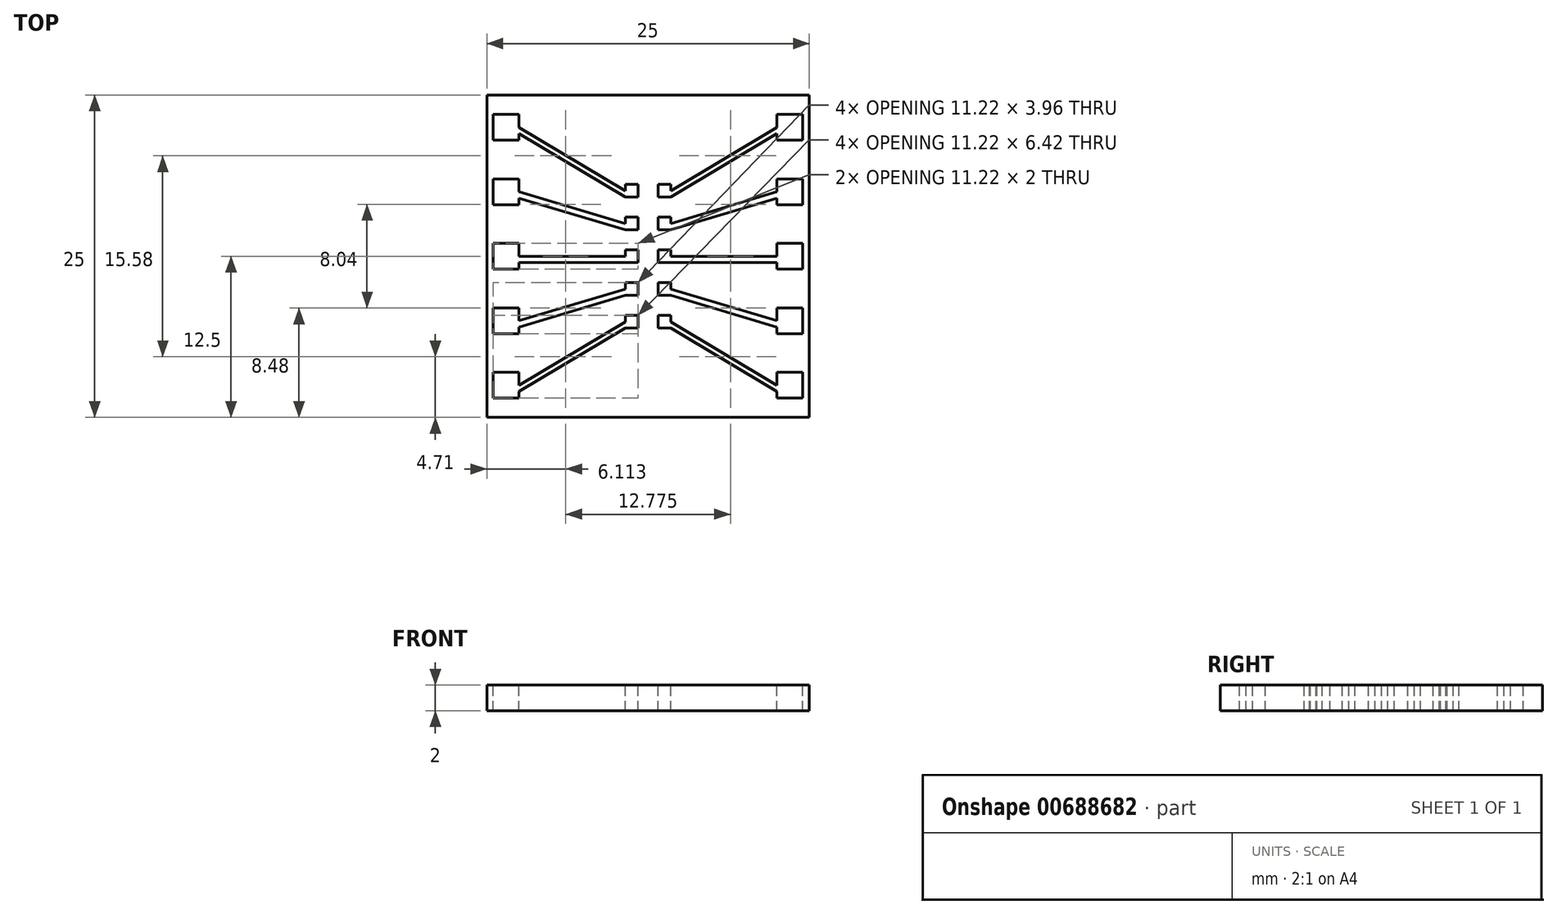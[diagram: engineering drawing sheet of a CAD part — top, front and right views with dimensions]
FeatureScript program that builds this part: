
annotation { "Feature Type Name" : "Feature", "Feature Type Description" : "" }
export const myFeature = defineFeature(function(context is Context, id is Id, definition is map)
    precondition{}
    {
        {
            var Q0;
            Q0=qCreatedBy(makeId("Top.planeOp"),FACE);
            var sketch = newSketch(context, id + "F0", { "sketchPlane" : qUnion([Q0])});
            skLineSegment(sketch, "E0.bottom", {"start": v(0, 0) * mm, "end": v(-25, 0) * mm});
            skLineSegment(sketch, "E0.top", {"start": v(0, 25) * mm, "end": v(-25, 25) * mm});
            skLineSegment(sketch, "E0.left", {"start": v(0, 0) * mm, "end": v(0, 25) * mm});
            skLineSegment(sketch, "E0.right", {"start": v(-25, 0) * mm, "end": v(-25, 25) * mm});
            skSolve(sketch);
        }
        {
            var Q0;
            Q0=makeQuery(id+"F0.imprint","IMPRINT",FACE,{"disambiguationData":[TD([[makeQuery(id+"F0.imprint","IMPRINT",EDGE,{"derivedFrom":sQuery(id+"F0.wireOp",EDGE,"E0.bottom")}),-1.0]])]});
            var Q1;
            Q1 = qSketchRegion(id + "F2", true);
            extrude(context, id + "F1", {"entities" : qUnion([Q0, Q1]), "depth" : 2 * mm, "offsetDistance" : 25 * mm});
        }
        {
            var Q0;
            Q0=makeQuery(id+"F1.opExtrude","CAP_FACE",FACE,{"disambiguationData":[OSD([sQuery(id+"F0.wireOp",EDGE,"E0.bottom"),sQuery(id+"F0.wireOp",EDGE,"E0.top"),sQuery(id+"F0.wireOp",EDGE,"E0.left"),sQuery(id+"F0.wireOp",EDGE,"E0.right")])],"isStart":false});
            var sketch = newSketch(context, id + "F2", { "sketchPlane" : qUnion([Q0])});
            skLineSegment(sketch, "E1.bottom", {"start": v(-14.28, 18.08) * mm, "end": v(-13.27, 18.08) * mm});
            skLineSegment(sketch, "E1.top", {"start": v(-14.28, 17.08) * mm, "end": v(-13.27, 17.08) * mm});
            skLineSegment(sketch, "E1.left", {"start": v(-14.27, 18.08) * mm, "end": v(-14.27, 17.58) * mm});
            skLineSegment(sketch, "E1.right", {"start": v(-13.27, 18.08) * mm, "end": v(-13.27, 17.08) * mm});
            skLineSegment(sketch, "E2.bottom", {"start": v(-24.5, 23.5) * mm, "end": v(-22.5, 23.5) * mm});
            skLineSegment(sketch, "E2.top", {"start": v(-24.5, 21.5) * mm, "end": v(-22.5, 21.5) * mm});
            skLineSegment(sketch, "E2.left", {"start": v(-24.5, 23.5) * mm, "end": v(-24.5, 21.5) * mm});
            skLineSegment(sketch, "E2.right", {"start": v(-22.5, 23.5) * mm, "end": v(-22.5, 22.5) * mm});
            skLineSegment(sketch, "E3.0.1.0", {"start": v(-14.28, 15.54) * mm, "end": v(-13.27, 15.54) * mm});
            skLineSegment(sketch, "E3.0.1.1", {"start": v(-14.28, 14.54) * mm, "end": v(-13.27, 14.54) * mm});
            skLineSegment(sketch, "E3.0.1.2", {"start": v(-14.27, 15.54) * mm, "end": v(-14.27, 15.04) * mm});
            skLineSegment(sketch, "E3.0.1.3", {"start": v(-13.27, 15.54) * mm, "end": v(-13.27, 14.54) * mm});
            skLineSegment(sketch, "E3.0.2.0", {"start": v(-14.28, 13) * mm, "end": v(-13.27, 13) * mm});
            skLineSegment(sketch, "E3.0.2.1", {"start": v(-14.28, 12) * mm, "end": v(-13.27, 12) * mm});
            skLineSegment(sketch, "E3.0.2.2", {"start": v(-14.28, 13) * mm, "end": v(-14.28, 12.5) * mm});
            skLineSegment(sketch, "E3.0.2.3", {"start": v(-13.28, 13) * mm, "end": v(-13.28, 12) * mm});
            skLineSegment(sketch, "E3.0.3.0", {"start": v(-14.28, 10.46) * mm, "end": v(-13.27, 10.46) * mm});
            skLineSegment(sketch, "E3.0.3.1", {"start": v(-14.28, 9.46) * mm, "end": v(-13.27, 9.46) * mm});
            skLineSegment(sketch, "E3.0.3.2", {"start": v(-14.28, 10.46) * mm, "end": v(-14.28, 9.96) * mm});
            skLineSegment(sketch, "E3.0.3.3", {"start": v(-13.28, 10.46) * mm, "end": v(-13.28, 9.46) * mm});
            skLineSegment(sketch, "E3.0.4.0", {"start": v(-14.28, 7.92) * mm, "end": v(-13.27, 7.92) * mm});
            skLineSegment(sketch, "E3.0.4.1", {"start": v(-14.28, 6.92) * mm, "end": v(-13.27, 6.92) * mm});
            skLineSegment(sketch, "E3.0.4.2", {"start": v(-14.28, 7.92) * mm, "end": v(-14.28, 7.42) * mm});
            skLineSegment(sketch, "E3.0.4.3", {"start": v(-13.28, 7.92) * mm, "end": v(-13.28, 6.92) * mm});
            skLineSegment(sketch, "E3.direction1", {"start": v(-14.28, 17.08) * mm, "end": v(0, 17.08) * mm, "construction": true});
            skLineSegment(sketch, "E3.direction2", {"start": v(-14.27, 17.08) * mm, "end": v(-14.27, 15.04) * mm, "construction": true});
            skLineSegment(sketch, "E4.0.1.0", {"start": v(-22.5, 18.5) * mm, "end": v(-22.5, 17.5) * mm});
            skLineSegment(sketch, "E4.0.1.1", {"start": v(-24.5, 18.5) * mm, "end": v(-22.5, 18.5) * mm});
            skLineSegment(sketch, "E4.0.1.2", {"start": v(-24.5, 16.5) * mm, "end": v(-22.5, 16.5) * mm});
            skLineSegment(sketch, "E4.0.1.3", {"start": v(-24.5, 18.5) * mm, "end": v(-24.5, 16.5) * mm});
            skLineSegment(sketch, "E4.0.2.0", {"start": v(-22.5, 13.5) * mm, "end": v(-22.5, 12.5) * mm});
            skLineSegment(sketch, "E4.0.2.1", {"start": v(-24.5, 13.5) * mm, "end": v(-22.5, 13.5) * mm});
            skLineSegment(sketch, "E4.0.2.2", {"start": v(-24.5, 11.5) * mm, "end": v(-22.5, 11.5) * mm});
            skLineSegment(sketch, "E4.0.2.3", {"start": v(-24.5, 13.5) * mm, "end": v(-24.5, 11.5) * mm});
            skLineSegment(sketch, "E4.0.3.0", {"start": v(-22.5, 8.5) * mm, "end": v(-22.5, 7.5) * mm});
            skLineSegment(sketch, "E4.0.3.1", {"start": v(-24.5, 8.5) * mm, "end": v(-22.5, 8.5) * mm});
            skLineSegment(sketch, "E4.0.3.2", {"start": v(-24.5, 6.5) * mm, "end": v(-22.5, 6.5) * mm});
            skLineSegment(sketch, "E4.0.3.3", {"start": v(-24.5, 8.5) * mm, "end": v(-24.5, 6.5) * mm});
            skLineSegment(sketch, "E4.0.4.0", {"start": v(-22.5, 3.5) * mm, "end": v(-22.5, 2.5) * mm});
            skLineSegment(sketch, "E4.0.4.1", {"start": v(-24.5, 3.5) * mm, "end": v(-22.5, 3.5) * mm});
            skLineSegment(sketch, "E4.0.4.2", {"start": v(-24.5, 1.5) * mm, "end": v(-22.5, 1.5) * mm});
            skLineSegment(sketch, "E4.0.4.3", {"start": v(-24.5, 3.5) * mm, "end": v(-24.5, 1.5) * mm});
            skLineSegment(sketch, "E4.direction1", {"start": v(-24.5, 21.5) * mm, "end": v(0, 21.5) * mm, "construction": true});
            skLineSegment(sketch, "E4.direction2", {"start": v(-24.5, 21.5) * mm, "end": v(-24.5, 16.5) * mm, "construction": true});
            skLineSegment(sketch, "E5", {"start": v(-22.5, 22.5) * mm, "end": v(-14.28, 17.58) * mm});
            skLineSegment(sketch, "E6", {"start": v(-14.28, 17.08) * mm, "end": v(-22.5, 22) * mm});
            skLineSegment(sketch, "E7", {"start": v(-22.5, 12.5) * mm, "end": v(-14.28, 12.5) * mm});
            skLineSegment(sketch, "E8", {"start": v(-14.28, 12) * mm, "end": v(-22.5, 12) * mm});
            skLineSegment(sketch, "E9", {"start": v(-22.5, 7.5) * mm, "end": v(-14.27, 9.96) * mm});
            skLineSegment(sketch, "E10", {"start": v(-14.28, 9.46) * mm, "end": v(-22.5, 7) * mm});
            skLineSegment(sketch, "E11", {"start": v(-22.5, 2.5) * mm, "end": v(-14.28, 7.42) * mm});
            skLineSegment(sketch, "E12", {"start": v(-14.28, 6.92) * mm, "end": v(-22.5, 2) * mm});
            skLineSegment(sketch, "E13.trimOffspring", {"start": v(-22.5, 7) * mm, "end": v(-22.5, 6.5) * mm});
            skLineSegment(sketch, "E14.trimOffspring", {"start": v(-22.5, 2) * mm, "end": v(-22.5, 1.5) * mm});
            skLineSegment(sketch, "E15.trimOffspring", {"start": v(-22.5, 12) * mm, "end": v(-22.5, 11.5) * mm});
            skLineSegment(sketch, "E16.trimOffspring", {"start": v(-22.5, 22) * mm, "end": v(-22.5, 21.5) * mm});
            skLineSegment(sketch, "E17", {"start": v(-22.5, 17.5) * mm, "end": v(-14.28, 15.04) * mm});
            skLineSegment(sketch, "E18", {"start": v(-14.28, 14.54) * mm, "end": v(-22.5, 17) * mm});
            skLineSegment(sketch, "E19.trimOffspring", {"start": v(-22.5, 17) * mm, "end": v(-22.5, 16.5) * mm});
            skLineSegment(sketch, "E20", {"start": v(-12.5, 25) * mm, "end": v(-12.5, 0) * mm, "construction": true});
            skLineSegment(sketch, "E21.MirrorCS", {"start": v(-10.72, 14.54) * mm, "end": v(-11.73, 14.54) * mm});
            skLineSegment(sketch, "E22.MirrorCS", {"start": v(-10.73, 15.54) * mm, "end": v(-10.73, 15.04) * mm});
            skLineSegment(sketch, "E23.MirrorCS", {"start": v(-10.72, 15.54) * mm, "end": v(-11.73, 15.54) * mm});
            skLineSegment(sketch, "E24.MirrorCS", {"start": v(-10.72, 10.46) * mm, "end": v(-11.73, 10.46) * mm});
            skLineSegment(sketch, "E25.MirrorCS", {"start": v(-10.72, 9.46) * mm, "end": v(-11.73, 9.46) * mm});
            skLineSegment(sketch, "E26.MirrorCS", {"start": v(-10.72, 12) * mm, "end": v(-11.73, 12) * mm});
            skLineSegment(sketch, "E27.MirrorCS", {"start": v(-10.73, 13) * mm, "end": v(-10.73, 12.5) * mm});
            skLineSegment(sketch, "E28.MirrorCS", {"start": v(-10.73, 18.08) * mm, "end": v(-11.73, 18.08) * mm});
            skLineSegment(sketch, "E29.MirrorCS", {"start": v(-10.73, 17.08) * mm, "end": v(-11.73, 17.08) * mm});
            skLineSegment(sketch, "E30.MirrorCS", {"start": v(-10.73, 18.08) * mm, "end": v(-10.73, 17.58) * mm});
            skLineSegment(sketch, "E31.MirrorCS", {"start": v(-10.72, 13) * mm, "end": v(-11.73, 13) * mm});
            skLineSegment(sketch, "E32.MirrorCS", {"start": v(-0.5, 21.5) * mm, "end": v(-0.5, 16.5) * mm, "construction": true});
            skLineSegment(sketch, "E33.MirrorCS", {"start": v(-10.73, 17.08) * mm, "end": v(-10.73, 15.04) * mm, "construction": true});
            skLineSegment(sketch, "E34.MirrorCS", {"start": v(-10.73, 10.46) * mm, "end": v(-10.73, 9.96) * mm});
            skLineSegment(sketch, "E35.MirrorCS", {"start": v(-2.5, 7) * mm, "end": v(-2.5, 6.5) * mm});
            skLineSegment(sketch, "E36.MirrorCS", {"start": v(-2.5, 2) * mm, "end": v(-2.5, 1.5) * mm});
            skLineSegment(sketch, "E37.MirrorCS", {"start": v(-0.5, 21.5) * mm, "end": v(-2.5, 21.5) * mm});
            skLineSegment(sketch, "E38.MirrorCS", {"start": v(-2.5, 8.5) * mm, "end": v(-2.5, 7.5) * mm});
            skLineSegment(sketch, "E39.MirrorCS", {"start": v(-2.5, 12) * mm, "end": v(-2.5, 11.5) * mm});
            skLineSegment(sketch, "E40.MirrorCS", {"start": v(-10.73, 7.92) * mm, "end": v(-10.73, 7.42) * mm});
            skLineSegment(sketch, "E41.MirrorCS", {"start": v(-2.5, 22) * mm, "end": v(-2.5, 21.5) * mm});
            skLineSegment(sketch, "E42.MirrorCS", {"start": v(-2.5, 17) * mm, "end": v(-2.5, 16.5) * mm});
            skLineSegment(sketch, "E43.MirrorCS", {"start": v(-10.72, 6.92) * mm, "end": v(-11.73, 6.92) * mm});
            skLineSegment(sketch, "E44.MirrorCS", {"start": v(-10.72, 7.92) * mm, "end": v(-11.73, 7.92) * mm});
            skLineSegment(sketch, "E45.MirrorCS", {"start": v(-11.73, 10.46) * mm, "end": v(-11.73, 9.46) * mm});
            skLineSegment(sketch, "E46.MirrorCS", {"start": v(-11.73, 13) * mm, "end": v(-11.73, 12) * mm});
            skLineSegment(sketch, "E47.MirrorCS", {"start": v(-2.5, 23.5) * mm, "end": v(-2.5, 22.5) * mm});
            skLineSegment(sketch, "E48.MirrorCS", {"start": v(-11.72, 15.54) * mm, "end": v(-11.72, 14.54) * mm});
            skLineSegment(sketch, "E49.MirrorCS", {"start": v(-2.5, 18.5) * mm, "end": v(-2.5, 17.5) * mm});
            skLineSegment(sketch, "E50.MirrorCS", {"start": v(-0.5, 16.5) * mm, "end": v(-2.5, 16.5) * mm});
            skLineSegment(sketch, "E51.MirrorCS", {"start": v(-2.5, 13.5) * mm, "end": v(-2.5, 12.5) * mm});
            skLineSegment(sketch, "E52.MirrorCS", {"start": v(-0.5, 6.5) * mm, "end": v(-2.5, 6.5) * mm});
            skLineSegment(sketch, "E53.MirrorCS", {"start": v(-11.73, 7.92) * mm, "end": v(-11.73, 6.92) * mm});
            skLineSegment(sketch, "E54.MirrorCS", {"start": v(-0.5, 11.5) * mm, "end": v(-2.5, 11.5) * mm});
            skLineSegment(sketch, "E55.MirrorCS", {"start": v(-0.5, 18.5) * mm, "end": v(-0.5, 16.5) * mm});
            skLineSegment(sketch, "E56.MirrorCS", {"start": v(-0.5, 3.5) * mm, "end": v(-2.5, 3.5) * mm});
            skLineSegment(sketch, "E57.MirrorCS", {"start": v(-0.5, 8.5) * mm, "end": v(-2.5, 8.5) * mm});
            skLineSegment(sketch, "E58.MirrorCS", {"start": v(-0.5, 13.5) * mm, "end": v(-0.5, 11.5) * mm});
            skLineSegment(sketch, "E59.MirrorCS", {"start": v(-11.72, 18.08) * mm, "end": v(-11.72, 17.08) * mm});
            skLineSegment(sketch, "E60.MirrorCS", {"start": v(-0.5, 23.5) * mm, "end": v(-2.5, 23.5) * mm});
            skLineSegment(sketch, "E61.MirrorCS", {"start": v(-0.5, 23.5) * mm, "end": v(-0.5, 21.5) * mm});
            skLineSegment(sketch, "E62.MirrorCS", {"start": v(-2.5, 3.5) * mm, "end": v(-2.5, 2.5) * mm});
            skLineSegment(sketch, "E63.MirrorCS", {"start": v(-0.5, 13.5) * mm, "end": v(-2.5, 13.5) * mm});
            skLineSegment(sketch, "E64.MirrorCS", {"start": v(-0.5, 3.5) * mm, "end": v(-0.5, 1.5) * mm});
            skLineSegment(sketch, "E65.MirrorCS", {"start": v(-0.5, 18.5) * mm, "end": v(-2.5, 18.5) * mm});
            skLineSegment(sketch, "E66.MirrorCS", {"start": v(-0.5, 8.5) * mm, "end": v(-0.5, 6.5) * mm});
            skLineSegment(sketch, "E67.MirrorCS", {"start": v(-0.5, 1.5) * mm, "end": v(-2.5, 1.5) * mm});
            skLineSegment(sketch, "E68.MirrorCS", {"start": v(-10.73, 17.08) * mm, "end": v(-2.5, 22) * mm});
            skLineSegment(sketch, "E69.MirrorCS", {"start": v(-2.5, 7.5) * mm, "end": v(-10.73, 9.96) * mm});
            skLineSegment(sketch, "E70.MirrorCS", {"start": v(-10.73, 6.92) * mm, "end": v(-2.5, 2) * mm});
            skLineSegment(sketch, "E71.MirrorCS", {"start": v(-2.5, 12.5) * mm, "end": v(-10.73, 12.5) * mm});
            skLineSegment(sketch, "E72.MirrorCS", {"start": v(-10.72, 9.46) * mm, "end": v(-2.5, 7) * mm});
            skLineSegment(sketch, "E73.MirrorCS", {"start": v(-10.73, 14.54) * mm, "end": v(-2.5, 17) * mm});
            skLineSegment(sketch, "E74.MirrorCS", {"start": v(-10.72, 12) * mm, "end": v(-2.5, 12) * mm});
            skLineSegment(sketch, "E75.MirrorCS", {"start": v(-2.5, 2.5) * mm, "end": v(-10.73, 7.42) * mm});
            skLineSegment(sketch, "E76.MirrorCS", {"start": v(-2.5, 22.5) * mm, "end": v(-10.73, 17.58) * mm});
            skLineSegment(sketch, "E77.MirrorCS", {"start": v(-2.5, 17.5) * mm, "end": v(-10.73, 15.04) * mm});
            skSolve(sketch);
        }
        {
            var Q0;
            Q0=makeQuery(id+"F2.imprint","IMPRINT",FACE,{"disambiguationData":[TD([[makeQuery(id+"F2.imprint","IMPRINT",EDGE,{"derivedFrom":sQuery(id+"F2.wireOp",EDGE,"E3.0.1.0")}),-1.0]])]});
            var Q1;
            Q1=makeQuery(id+"F2.imprint","IMPRINT",FACE,{"disambiguationData":[TD([[makeQuery(id+"F2.imprint","IMPRINT",EDGE,{"derivedFrom":sQuery(id+"F2.wireOp",EDGE,"E1.bottom")}),-1.0]])]});
            var Q2;
            Q2=makeQuery(id+"F2.imprint","IMPRINT",FACE,{"disambiguationData":[TD([[makeQuery(id+"F2.imprint","IMPRINT",EDGE,{"derivedFrom":sQuery(id+"F2.wireOp",EDGE,"E3.0.2.0")}),-1.0]])]});
            var Q3;
            Q3=makeQuery(id+"F2.imprint","IMPRINT",FACE,{"disambiguationData":[TD([[makeQuery(id+"F2.imprint","IMPRINT",EDGE,{"derivedFrom":sQuery(id+"F2.wireOp",EDGE,"E3.0.3.0")}),-1.0]])]});
            var Q4;
            Q4=makeQuery(id+"F2.imprint","IMPRINT",FACE,{"disambiguationData":[TD([[makeQuery(id+"F2.imprint","IMPRINT",EDGE,{"derivedFrom":sQuery(id+"F2.wireOp",EDGE,"E3.0.4.0")}),-1.0]])]});
            var Q5;
            Q5=makeQuery(id+"F2.imprint","IMPRINT",FACE,{"disambiguationData":[TD([[makeQuery(id+"F2.imprint","IMPRINT",EDGE,{"derivedFrom":sQuery(id+"F2.wireOp",EDGE,"E36.MirrorCS")}),1.0]])]});
            var Q6;
            Q6=makeQuery(id+"F2.imprint","IMPRINT",FACE,{"disambiguationData":[TD([[makeQuery(id+"F2.imprint","IMPRINT",EDGE,{"derivedFrom":sQuery(id+"F2.wireOp",EDGE,"E26.MirrorCS")}),-1.0]])]});
            var Q7;
            Q7=makeQuery(id+"F2.imprint","IMPRINT",FACE,{"disambiguationData":[TD([[makeQuery(id+"F2.imprint","IMPRINT",EDGE,{"derivedFrom":sQuery(id+"F2.wireOp",EDGE,"E21.MirrorCS")}),-1.0]])]});
            var Q8;
            Q8=makeQuery(id+"F2.imprint","IMPRINT",FACE,{"disambiguationData":[TD([[makeQuery(id+"F2.imprint","IMPRINT",EDGE,{"derivedFrom":sQuery(id+"F2.wireOp",EDGE,"E28.MirrorCS")}),1.0]])]});
            var Q9;
            Q9=makeQuery(id+"F2.imprint","IMPRINT",FACE,{"disambiguationData":[TD([[makeQuery(id+"F2.imprint","IMPRINT",EDGE,{"derivedFrom":sQuery(id+"F2.wireOp",EDGE,"E24.MirrorCS")}),1.0]])]});
            var Q10;
            Q10=sQuery(id+"F2.wireOp",EDGE,"E50.MirrorCS");
            var Q11;
            Q11=sQuery(id+"F2.wireOp",EDGE,"E66.MirrorCS");
            var Q12;
            Q12=sQuery(id+"F2.wireOp",EDGE,"E64.MirrorCS");
            var Q13;
            Q13=sQuery(id+"F2.wireOp",EDGE,"E7");
            var Q14;
            Q14=sQuery(id+"F2.wireOp",EDGE,"E4.0.1.2");
            var Q15;
            Q15=sQuery(id+"F2.wireOp",EDGE,"E4.0.4.1");
            var Q16;
            Q16=sQuery(id+"F2.wireOp",EDGE,"E4.0.4.2");
            var Q17;
            Q17=sQuery(id+"F2.wireOp",EDGE,"E69.MirrorCS");
            var Q18;
            Q18=sQuery(id+"F2.wireOp",EDGE,"E17");
            var Q19;
            Q19=sQuery(id+"F2.wireOp",EDGE,"E70.MirrorCS");
            var Q20;
            Q20=sQuery(id+"F2.wireOp",EDGE,"E67.MirrorCS");
            var Q21;
            Q21=sQuery(id+"F2.wireOp",EDGE,"E63.MirrorCS");
            var Q22;
            Q22=sQuery(id+"F2.wireOp",EDGE,"E5");
            var Q23;
            Q23=sQuery(id+"F2.wireOp",EDGE,"E4.0.3.3");
            var Q24;
            Q24=sQuery(id+"F2.wireOp",EDGE,"E6");
            var Q25;
            Q25=sQuery(id+"F2.wireOp",EDGE,"E71.MirrorCS");
            var Q26;
            Q26=sQuery(id+"F2.wireOp",EDGE,"E77.MirrorCS");
            var Q27;
            Q27=sQuery(id+"F2.wireOp",EDGE,"E4.0.4.3");
            var Q28;
            Q28=sQuery(id+"F2.wireOp",EDGE,"E18");
            var Q29;
            Q29=sQuery(id+"F2.wireOp",EDGE,"E61.MirrorCS");
            var Q30;
            Q30=sQuery(id+"F2.wireOp",EDGE,"E4.0.3.2");
            var Q31;
            Q31=sQuery(id+"F2.wireOp",EDGE,"E2.left");
            var Q32;
            Q32=sQuery(id+"F2.wireOp",EDGE,"E76.MirrorCS");
            var Q33;
            Q33=sQuery(id+"F2.wireOp",EDGE,"E4.0.1.1");
            var Q34;
            Q34=sQuery(id+"F2.wireOp",EDGE,"E12");
            var Q35;
            Q35=sQuery(id+"F2.wireOp",EDGE,"E2.bottom");
            var Q36;
            Q36=sQuery(id+"F2.wireOp",EDGE,"E60.MirrorCS");
            var Q37;
            Q37=sQuery(id+"F2.wireOp",EDGE,"E4.0.3.1");
            var Q38;
            Q38=sQuery(id+"F2.wireOp",EDGE,"E75.MirrorCS");
            var Q39;
            Q39=sQuery(id+"F2.wireOp",EDGE,"E11");
            var Q40;
            Q40=sQuery(id+"F2.wireOp",EDGE,"E54.MirrorCS");
            var Q41;
            Q41=sQuery(id+"F2.wireOp",EDGE,"E10");
            var Q42;
            Q42=sQuery(id+"F2.wireOp",EDGE,"E58.MirrorCS");
            var Q43;
            Q43=sQuery(id+"F2.wireOp",EDGE,"E4.0.2.3");
            var Q44;
            Q44=sQuery(id+"F2.wireOp",EDGE,"E65.MirrorCS");
            var Q45;
            Q45=sQuery(id+"F2.wireOp",EDGE,"E74.MirrorCS");
            var Q46;
            Q46=sQuery(id+"F2.wireOp",EDGE,"E4.0.2.2");
            var Q47;
            Q47=sQuery(id+"F2.wireOp",EDGE,"E73.MirrorCS");
            var Q48;
            Q48=sQuery(id+"F2.wireOp",EDGE,"E9");
            var Q49;
            Q49=sQuery(id+"F2.wireOp",EDGE,"E57.MirrorCS");
            var Q50;
            Q50=sQuery(id+"F2.wireOp",EDGE,"E72.MirrorCS");
            var Q51;
            Q51=sQuery(id+"F2.wireOp",EDGE,"E8");
            var Q52;
            Q52=sQuery(id+"F2.wireOp",EDGE,"E52.MirrorCS");
            var Q53;
            Q53=sQuery(id+"F2.wireOp",EDGE,"E56.MirrorCS");
            var Q54;
            Q54=sQuery(id+"F2.wireOp",EDGE,"E4.0.2.1");
            var Q55;
            Q55=sQuery(id+"F2.wireOp",EDGE,"E68.MirrorCS");
            var Q56;
            Q56=sQuery(id+"F2.wireOp",EDGE,"E37.MirrorCS");
            var Q57;
            Q57=sQuery(id+"F2.wireOp",EDGE,"E55.MirrorCS");
            var Q58;
            Q58=sQuery(id+"F2.wireOp",EDGE,"E2.top");
            var Q59;
            Q59=sQuery(id+"F2.wireOp",EDGE,"E4.0.1.3");
            var Q60;
            Q60=sQuery(id+"F2.wireOp",EDGE,"E39.MirrorCS");
            var Q61;
            Q61=sQuery(id+"F2.wireOp",EDGE,"E21.MirrorCS");
            var Q62;
            Q62=sQuery(id+"F2.wireOp",EDGE,"E23.MirrorCS");
            var Q63;
            Q63=sQuery(id+"F2.wireOp",EDGE,"E48.MirrorCS");
            var Q64;
            Q64=sQuery(id+"F2.wireOp",EDGE,"E3.0.4.3");
            var Q65;
            Q65=sQuery(id+"F2.wireOp",EDGE,"E31.MirrorCS");
            var Q66;
            Q66=sQuery(id+"F2.wireOp",EDGE,"E51.MirrorCS");
            var Q67;
            Q67=sQuery(id+"F2.wireOp",EDGE,"E47.MirrorCS");
            var Q68;
            Q68=sQuery(id+"F2.wireOp",EDGE,"E4.0.1.0");
            var Q69;
            Q69=sQuery(id+"F2.wireOp",EDGE,"E4.0.4.0");
            var Q70;
            Q70=sQuery(id+"F2.wireOp",EDGE,"E19.trimOffspring");
            var Q71;
            Q71=sQuery(id+"F2.wireOp",EDGE,"E35.MirrorCS");
            var Q72;
            Q72=sQuery(id+"F2.wireOp",EDGE,"E14.trimOffspring");
            var Q73;
            Q73=sQuery(id+"F2.wireOp",EDGE,"E46.MirrorCS");
            var Q74;
            Q74=sQuery(id+"F2.wireOp",EDGE,"E62.MirrorCS");
            var Q75;
            Q75=sQuery(id+"F2.wireOp",EDGE,"E3.0.4.1");
            var Q76;
            Q76=sQuery(id+"F2.wireOp",EDGE,"E4.0.2.0");
            var Q77;
            Q77=sQuery(id+"F2.wireOp",EDGE,"E53.MirrorCS");
            var Q78;
            Q78=sQuery(id+"F2.wireOp",EDGE,"E3.0.2.0");
            var Q79;
            Q79=sQuery(id+"F2.wireOp",EDGE,"E13.trimOffspring");
            var Q80;
            Q80=sQuery(id+"F2.wireOp",EDGE,"E3.0.1.3");
            var Q81;
            Q81=sQuery(id+"F2.wireOp",EDGE,"E34.MirrorCS");
            var Q82;
            Q82=sQuery(id+"F2.wireOp",EDGE,"E29.MirrorCS");
            var Q83;
            Q83=sQuery(id+"F2.wireOp",EDGE,"E45.MirrorCS");
            var Q84;
            Q84=sQuery(id+"F2.wireOp",EDGE,"E3.0.1.1");
            var Q85;
            Q85=sQuery(id+"F2.wireOp",EDGE,"E3.0.4.0");
            var Q86;
            Q86=sQuery(id+"F2.wireOp",EDGE,"E3.0.1.0");
            var Q87;
            Q87=sQuery(id+"F2.wireOp",EDGE,"E2.right");
            var Q88;
            Q88=sQuery(id+"F2.wireOp",EDGE,"E28.MirrorCS");
            var Q89;
            Q89=sQuery(id+"F2.wireOp",EDGE,"E44.MirrorCS");
            var Q90;
            Q90=sQuery(id+"F2.wireOp",EDGE,"E1.right");
            var Q91;
            Q91=sQuery(id+"F2.wireOp",EDGE,"E3.0.3.3");
            var Q92;
            Q92=sQuery(id+"F2.wireOp",EDGE,"E38.MirrorCS");
            var Q93;
            Q93=sQuery(id+"F2.wireOp",EDGE,"E1.left");
            var Q94;
            Q94=sQuery(id+"F2.wireOp",EDGE,"E1.top");
            var Q95;
            Q95=sQuery(id+"F2.wireOp",EDGE,"E43.MirrorCS");
            var Q96;
            Q96=sQuery(id+"F2.wireOp",EDGE,"E59.MirrorCS");
            var Q97;
            Q97=sQuery(id+"F2.wireOp",EDGE,"E1.bottom");
            var Q98;
            Q98=sQuery(id+"F2.wireOp",EDGE,"E3.0.2.3");
            var Q99;
            Q99=sQuery(id+"F2.wireOp",EDGE,"E4.0.3.0");
            var Q100;
            Q100=sQuery(id+"F2.wireOp",EDGE,"E3.0.2.2");
            var Q101;
            Q101=sQuery(id+"F2.wireOp",EDGE,"E3.0.2.1");
            var Q102;
            Q102=sQuery(id+"F2.wireOp",EDGE,"E26.MirrorCS");
            var Q103;
            Q103=sQuery(id+"F2.wireOp",EDGE,"E49.MirrorCS");
            var Q104;
            Q104=sQuery(id+"F2.wireOp",EDGE,"E42.MirrorCS");
            var Q105;
            Q105=sQuery(id+"F2.wireOp",EDGE,"E3.0.3.1");
            var Q106;
            Q106=sQuery(id+"F2.wireOp",EDGE,"E3.0.3.0");
            var Q107;
            Q107=sQuery(id+"F2.wireOp",EDGE,"E25.MirrorCS");
            var Q108;
            Q108=sQuery(id+"F2.wireOp",EDGE,"E24.MirrorCS");
            var Q109;
            Q109=sQuery(id+"F2.wireOp",EDGE,"E40.MirrorCS");
            var Q110;
            Q110=sQuery(id+"F2.wireOp",EDGE,"E36.MirrorCS");
            var Q111;
            Q111=sQuery(id+"F2.wireOp",EDGE,"E15.trimOffspring");
            var Q112;
            Q112=sQuery(id+"F2.wireOp",EDGE,"E3.0.4.2");
            var Q113;
            Q113=sQuery(id+"F2.wireOp",EDGE,"E30.MirrorCS");
            var Q114;
            Q114=sQuery(id+"F2.wireOp",EDGE,"E3.0.1.2");
            var Q115;
            Q115=sQuery(id+"F2.wireOp",EDGE,"E22.MirrorCS");
            var Q116;
            Q116=sQuery(id+"F2.wireOp",EDGE,"E27.MirrorCS");
            var Q117;
            Q117=sQuery(id+"F2.wireOp",EDGE,"E3.0.3.2");
            var Q118;
            Q118=sQuery(id+"F2.wireOp",EDGE,"E41.MirrorCS");
            var Q119;
            Q119=sQuery(id+"F2.wireOp",EDGE,"E16.trimOffspring");
            extrude(context, id + "F3", {"entities" : qUnion([Q0, Q1, Q2, Q3, Q4, Q5, Q6, Q7, Q8, Q9]), "operationType" : NewBodyOperationType.REMOVE, "surfaceEntities" : qUnion([Q10, Q11, Q12, Q13, Q14, Q15, Q16, Q17, Q18, Q19, Q20, Q21, Q22, Q23, Q24, Q25, Q26, Q27, Q28, Q29, Q30, Q31, Q32, Q33, Q34, Q35, Q36, Q37, Q38, Q39, Q40, Q41, Q42, Q43, Q44, Q45, Q46, Q47, Q48, Q49, Q50, Q51, Q52, Q53, Q54, Q55, Q56, Q57, Q58, Q59, Q60, Q61, Q62, Q63, Q64, Q65, Q66, Q67, Q68, Q69, Q70, Q71, Q72, Q73, Q74, Q75, Q76, Q77, Q78, Q79, Q80, Q81, Q82, Q83, Q84, Q85, Q86, Q87, Q88, Q89, Q90, Q91, Q92, Q93, Q94, Q95, Q96, Q97, Q98, Q99, Q100, Q101, Q102, Q103, Q104, Q105, Q106, Q107, Q108, Q109, Q110, Q111, Q112, Q113, Q114, Q115, Q116, Q117, Q118, Q119]), "oppositeDirection" : true, "depth" : 2 * mm, "offsetDistance" : 25 * mm});
        }
    });
